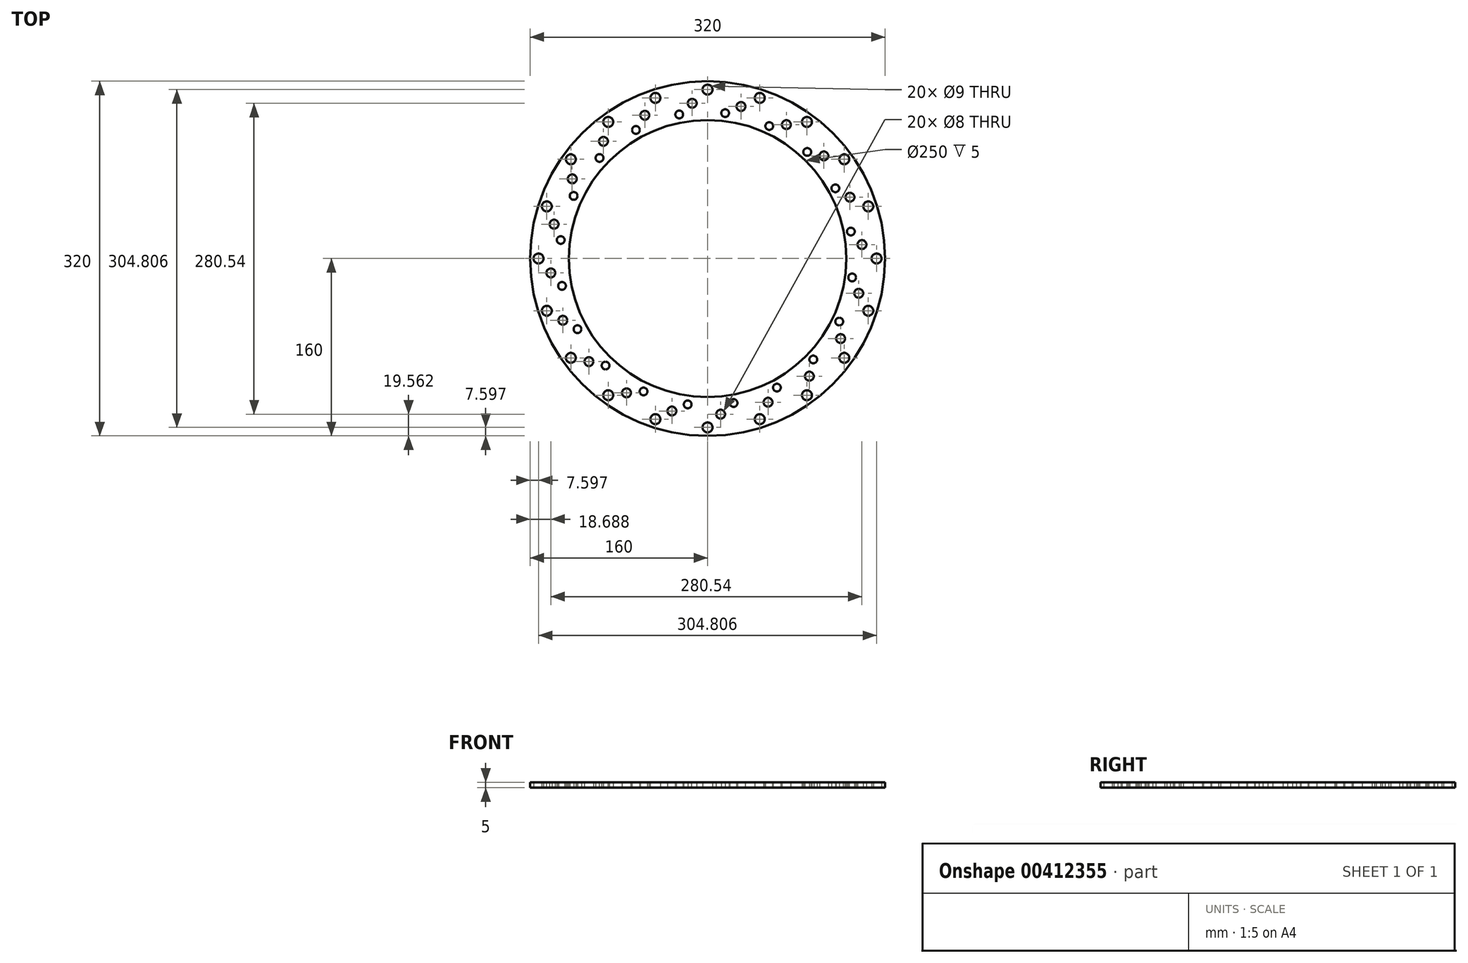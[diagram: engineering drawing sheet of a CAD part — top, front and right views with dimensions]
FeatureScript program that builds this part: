
annotation { "Feature Type Name" : "Feature", "Feature Type Description" : "" }
export const myFeature = defineFeature(function(context is Context, id is Id, definition is map)
    precondition{}
    {
        {
            var Q0;
            Q0=qCreatedBy(makeId("Top.planeOp"),FACE);
            var sketch = newSketch(context, id + "F0", { "sketchPlane" : qUnion([Q0])});
            skCircle(sketch, "E0", {"center": v(0, 0) * mm, "radius": 160 * mm});
            skCircle(sketch, "E1", {"center": v(0, 0) * mm, "radius": 125 * mm});
            skLineSegment(sketch, "E2", {"start": v(-230.5, 0) * mm, "end": v(307.33, 0) * mm, "construction": true});
            skLineSegment(sketch, "E3", {"start": v(0, 250.08) * mm, "end": v(0, -283.96) * mm, "construction": true});
            skCircle(sketch, "E4", {"center": v(0, 152.4) * mm, "radius": 4.5 * mm});
            skCircle(sketch, "E5.1.0", {"center": v(-47.1, 144.94) * mm, "radius": 4.5 * mm});
            skCircle(sketch, "E5.2.0", {"center": v(-89.58, 123.3) * mm, "radius": 4.5 * mm});
            skCircle(sketch, "E5.3.0", {"center": v(-123.3, 89.58) * mm, "radius": 4.5 * mm});
            skCircle(sketch, "E5.4.0", {"center": v(-144.94, 47.1) * mm, "radius": 4.5 * mm});
            skCircle(sketch, "E5.5.0", {"center": v(-152.4, 0) * mm, "radius": 4.5 * mm});
            skCircle(sketch, "E5.6.0", {"center": v(-144.94, -47.1) * mm, "radius": 4.5 * mm});
            skCircle(sketch, "E5.7.0", {"center": v(-123.3, -89.58) * mm, "radius": 4.5 * mm});
            skCircle(sketch, "E5.8.0", {"center": v(-89.58, -123.3) * mm, "radius": 4.5 * mm});
            skCircle(sketch, "E5.9.0", {"center": v(-47.1, -144.94) * mm, "radius": 4.5 * mm});
            skCircle(sketch, "E5.10.0", {"center": v(0, -152.4) * mm, "radius": 4.5 * mm});
            skCircle(sketch, "E5.11.0", {"center": v(47.1, -144.94) * mm, "radius": 4.5 * mm});
            skCircle(sketch, "E5.12.0", {"center": v(89.58, -123.3) * mm, "radius": 4.5 * mm});
            skCircle(sketch, "E5.13.0", {"center": v(123.3, -89.58) * mm, "radius": 4.5 * mm});
            skCircle(sketch, "E5.14.0", {"center": v(144.94, -47.1) * mm, "radius": 4.5 * mm});
            skCircle(sketch, "E5.15.0", {"center": v(152.4, 0) * mm, "radius": 4.5 * mm});
            skCircle(sketch, "E5.16.0", {"center": v(144.94, 47.1) * mm, "radius": 4.5 * mm});
            skCircle(sketch, "E5.17.0", {"center": v(123.3, 89.58) * mm, "radius": 4.5 * mm});
            skCircle(sketch, "E5.18.0", {"center": v(89.58, 123.3) * mm, "radius": 4.5 * mm});
            skCircle(sketch, "E5.19.0", {"center": v(47.1, 144.94) * mm, "radius": 4.5 * mm});
            skLineSegment(sketch, "E6", {"start": v(0, 0) * mm, "end": v(-53.5, 165.4) * mm, "construction": true});
            skLineSegment(sketch, "E7", {"start": v(-38.47, 118.93) * mm, "end": v(31.82, 179.4) * mm, "construction": true});
            skCircle(sketch, "E8", {"center": v(-13.86, 140.1) * mm, "radius": 4 * mm});
            skCircle(sketch, "E9", {"center": v(-25.57, 130.03) * mm, "radius": 3.5 * mm});
            skCircle(sketch, "E10.1.0", {"center": v(-56.58, 129.28) * mm, "radius": 4 * mm});
            skCircle(sketch, "E10.1.1", {"center": v(-64.6, 116.08) * mm, "radius": 3.5 * mm});
            skCircle(sketch, "E10.2.0", {"center": v(-93.86, 105.78) * mm, "radius": 4 * mm});
            skCircle(sketch, "E10.2.1", {"center": v(-97.41, 90.75) * mm, "radius": 3.5 * mm});
            skCircle(sketch, "E10.3.0", {"center": v(-122.06, 71.91) * mm, "radius": 4 * mm});
            skCircle(sketch, "E10.3.1", {"center": v(-120.79, 56.52) * mm, "radius": 3.5 * mm});
            skCircle(sketch, "E10.4.0", {"center": v(-138.4, 30.99) * mm, "radius": 4 * mm});
            skCircle(sketch, "E10.4.1", {"center": v(-132.45, 16.74) * mm, "radius": 3.5 * mm});
            skCircle(sketch, "E10.5.0", {"center": v(-141.31, -12.99) * mm, "radius": 4 * mm});
            skCircle(sketch, "E10.5.1", {"center": v(-131.24, -24.7) * mm, "radius": 3.5 * mm});
            skCircle(sketch, "E10.6.0", {"center": v(-130.49, -55.7) * mm, "radius": 4 * mm});
            skCircle(sketch, "E10.6.1", {"center": v(-117.29, -63.73) * mm, "radius": 3.5 * mm});
            skCircle(sketch, "E10.7.0", {"center": v(-106.99, -92.99) * mm, "radius": 4 * mm});
            skCircle(sketch, "E10.7.1", {"center": v(-91.96, -96.54) * mm, "radius": 3.5 * mm});
            skCircle(sketch, "E10.8.0", {"center": v(-73.12, -121.18) * mm, "radius": 4 * mm});
            skCircle(sketch, "E10.8.1", {"center": v(-57.73, -119.92) * mm, "radius": 3.5 * mm});
            skCircle(sketch, "E10.9.0", {"center": v(-32.2, -137.53) * mm, "radius": 4 * mm});
            skCircle(sketch, "E10.9.1", {"center": v(-17.95, -131.57) * mm, "radius": 3.5 * mm});
            skCircle(sketch, "E10.10.0", {"center": v(11.78, -140.44) * mm, "radius": 4 * mm});
            skCircle(sketch, "E10.10.1", {"center": v(23.49, -130.36) * mm, "radius": 3.5 * mm});
            skCircle(sketch, "E10.11.0", {"center": v(54.5, -129.61) * mm, "radius": 4 * mm});
            skCircle(sketch, "E10.11.1", {"center": v(62.52, -116.41) * mm, "radius": 3.5 * mm});
            skCircle(sketch, "E10.12.0", {"center": v(91.78, -106.11) * mm, "radius": 4 * mm});
            skCircle(sketch, "E10.12.1", {"center": v(95.33, -91.08) * mm, "radius": 3.5 * mm});
            skCircle(sketch, "E10.13.0", {"center": v(119.97, -72.25) * mm, "radius": 4 * mm});
            skCircle(sketch, "E10.13.1", {"center": v(118.7, -56.85) * mm, "radius": 3.5 * mm});
            skCircle(sketch, "E10.14.0", {"center": v(136.32, -31.32) * mm, "radius": 4 * mm});
            skCircle(sketch, "E10.14.1", {"center": v(130.36, -17.07) * mm, "radius": 3.5 * mm});
            skCircle(sketch, "E10.15.0", {"center": v(139.23, 12.65) * mm, "radius": 4 * mm});
            skCircle(sketch, "E10.15.1", {"center": v(129.15, 24.36) * mm, "radius": 3.5 * mm});
            skCircle(sketch, "E10.16.0", {"center": v(128.4, 55.37) * mm, "radius": 4 * mm});
            skCircle(sketch, "E10.16.1", {"center": v(115.2, 63.4) * mm, "radius": 3.5 * mm});
            skCircle(sketch, "E10.17.0", {"center": v(104.9, 92.65) * mm, "radius": 4 * mm});
            skCircle(sketch, "E10.17.1", {"center": v(89.87, 96.2) * mm, "radius": 3.5 * mm});
            skCircle(sketch, "E10.18.0", {"center": v(71.04, 120.85) * mm, "radius": 4 * mm});
            skCircle(sketch, "E10.18.1", {"center": v(55.64, 119.58) * mm, "radius": 3.5 * mm});
            skCircle(sketch, "E10.19.0", {"center": v(30.11, 137.2) * mm, "radius": 4 * mm});
            skCircle(sketch, "E10.19.1", {"center": v(15.86, 131.24) * mm, "radius": 3.5 * mm});
            skPoint(sketch, "E10.center", {"position": v(-1.04, -0.17) * mm});
            skSolve(sketch);
        }
        {
            var Q0;
            Q0=makeQuery(id+"F0.imprint","IMPRINT",FACE,{"disambiguationData":[TD([[makeQuery(id+"F0.imprint","IMPRINT",EDGE,{"derivedFrom":sQuery(id+"F0.wireOp",EDGE,"E0")}),1.0]])]});
            extrude(context, id + "F1", {"entities" : qUnion([Q0]), "depth" : 5 * mm});
        }
    });
